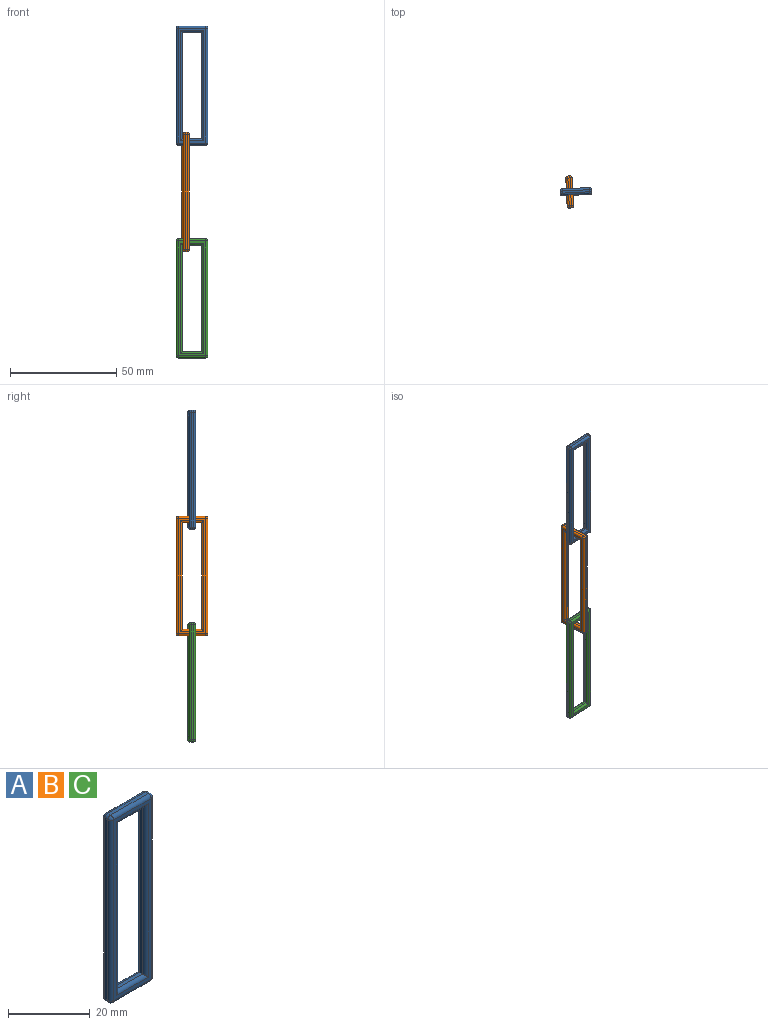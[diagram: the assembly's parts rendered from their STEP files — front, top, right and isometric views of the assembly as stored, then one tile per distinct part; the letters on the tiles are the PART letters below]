
ASSEMBLY  parts=3 mates=5
PART A: 38 faces, bbox 15x3x56 mm
  f0: plane 13x1mm, normal (0,0,1), area 13mm2, adj f18,f23,f26,f29
  f1: plane 54x1mm, normal (-1,0,0), area 54mm2, adj f15,f24,f25,f29
  f2: plane 13x1mm, normal (0,0,-1), area 13mm2, adj f10,f14,f15,f16
  f3: plane 50x1mm, normal (1,0,0), area 50mm2, adj f4,f6,f31,f35
  f4: plane 9x1mm, normal (0,0,-1), area 9mm2, adj f3,f5,f30,f34
  f5: plane 50x1mm, normal (-1,0,0), area 50mm2, adj f4,f6,f32,f36
  f6: plane 9x1mm, normal (0,0,1), area 9mm2, adj f3,f5,f33,f37
  f7: plane 54x1mm, normal (1,0,0), area 54mm2, adj f10,f13,f17,f18
  f8: plane 54x13mm, normal (0,-1,0), area 130mm2, adj f13,f14,f23,f24,f34,f35,f36,f37
  f9: plane 54x13mm, normal (0,1,0), area 130mm2, adj f16,f17,f25,f26,f30,f31,f32,f33
  f10: cylinder r=1mm len=1mm, axis (0,-1,0), area 1.6mm2, adj f2,f7,f11,f12
  f11: sphere r=1mm, area 1.6mm2, adj f10,f13,f14
  f12: sphere r=1mm, area 1.6mm2, adj f10,f16,f17
  f13: cylinder r=1mm len=54mm, axis (0,0,-1), area 84.8mm2, adj f7,f8,f11,f19
  f14: cylinder r=1mm len=13mm, axis (-1,0,0), area 20.4mm2, adj f2,f8,f11,f20
  f15: cylinder r=1mm len=1mm, axis (0,1,0), area 1.6mm2, adj f1,f2,f20,f21
  f16: cylinder r=1mm len=13mm, axis (1,0,0), area 20.4mm2, adj f2,f9,f12,f21
  f17: cylinder r=1mm len=54mm, axis (0,0,1), area 84.8mm2, adj f7,f9,f12,f22
  f18: cylinder r=1mm len=1mm, axis (0,1,0), area 1.6mm2, adj f0,f7,f19,f22
  f19: sphere r=1mm, area 1.6mm2, adj f13,f18,f23
  f20: sphere r=1mm, area 1.6mm2, adj f14,f15,f24
  f21: sphere r=1mm, area 1.6mm2, adj f15,f16,f25
  f22: sphere r=1mm, area 1.6mm2, adj f17,f18,f26
  f23: cylinder r=1mm len=13mm, axis (1,0,0), area 20.4mm2, adj f0,f8,f19,f27
  f24: cylinder r=1mm len=54mm, axis (0,0,1), area 84.8mm2, adj f1,f8,f20,f27
  f25: cylinder r=1mm len=54mm, axis (0,0,-1), area 84.8mm2, adj f1,f9,f21,f28
  f26: cylinder r=1mm len=13mm, axis (-1,0,0), area 20.4mm2, adj f0,f9,f22,f28
  f27: sphere r=1mm, area 1.6mm2, adj f23,f24,f29
  f28: sphere r=1mm, area 1.6mm2, adj f25,f26,f29
  f29: cylinder r=1mm len=1mm, axis (0,-1,0), area 1.6mm2, adj f0,f1,f27,f28
  f30: cylinder r=1mm len=11mm, axis (1,0,0), area 15.3mm2, adj f4,f9,f31,f32
  f31: cylinder r=1mm len=52mm, axis (0,0,1), area 79.7mm2, adj f3,f9,f30,f33
  f32: cylinder r=1mm len=52mm, axis (0,0,-1), area 79.7mm2, adj f5,f9,f30,f33
  f33: cylinder r=1mm len=11mm, axis (-1,0,0), area 15.3mm2, adj f6,f9,f31,f32
  f34: cylinder r=1mm len=11mm, axis (-1,0,0), area 15.3mm2, adj f4,f8,f35,f36
  f35: cylinder r=1mm len=52mm, axis (0,0,-1), area 79.7mm2, adj f3,f8,f34,f37
  f36: cylinder r=1mm len=52mm, axis (0,0,1), area 79.7mm2, adj f5,f8,f34,f37
  f37: cylinder r=1mm len=11mm, axis (1,0,0), area 15.3mm2, adj f6,f8,f35,f36
PART B: same geometry as A
PART C: same geometry as A
PLACE A rot(axis=(0,0,1),2.8deg) t=(5.85,0.27,95.31)mm
PLACE B rot(axis=(0,0,1),92.8deg) t=(1.43,-1.44,45.31)mm
PLACE C rot(axis=(0,0,1),2.8deg) t=(5.85,0.27,-4.69)mm
MATE planar A.f6 <-> B.f4  axis (0,0,1) through (5.95,-1.72,70.31)mm
MATE planar C.f4 <-> B.f6  axis (0,0,-1) through (5.93,-1.22,20.31)mm
MATE planar C.f3 <-> B.f9  axis (1,0.05,0) through (1.43,-1.44,-4.69)mm
MATE parallel B.f8 <-> C.f7  axis (1,0.05,0) through (4.43,-1.3,45.31)mm
MATE planar A.f3 <-> B.f9  axis (1,0.05,0) through (1.43,-1.44,95.31)mm
